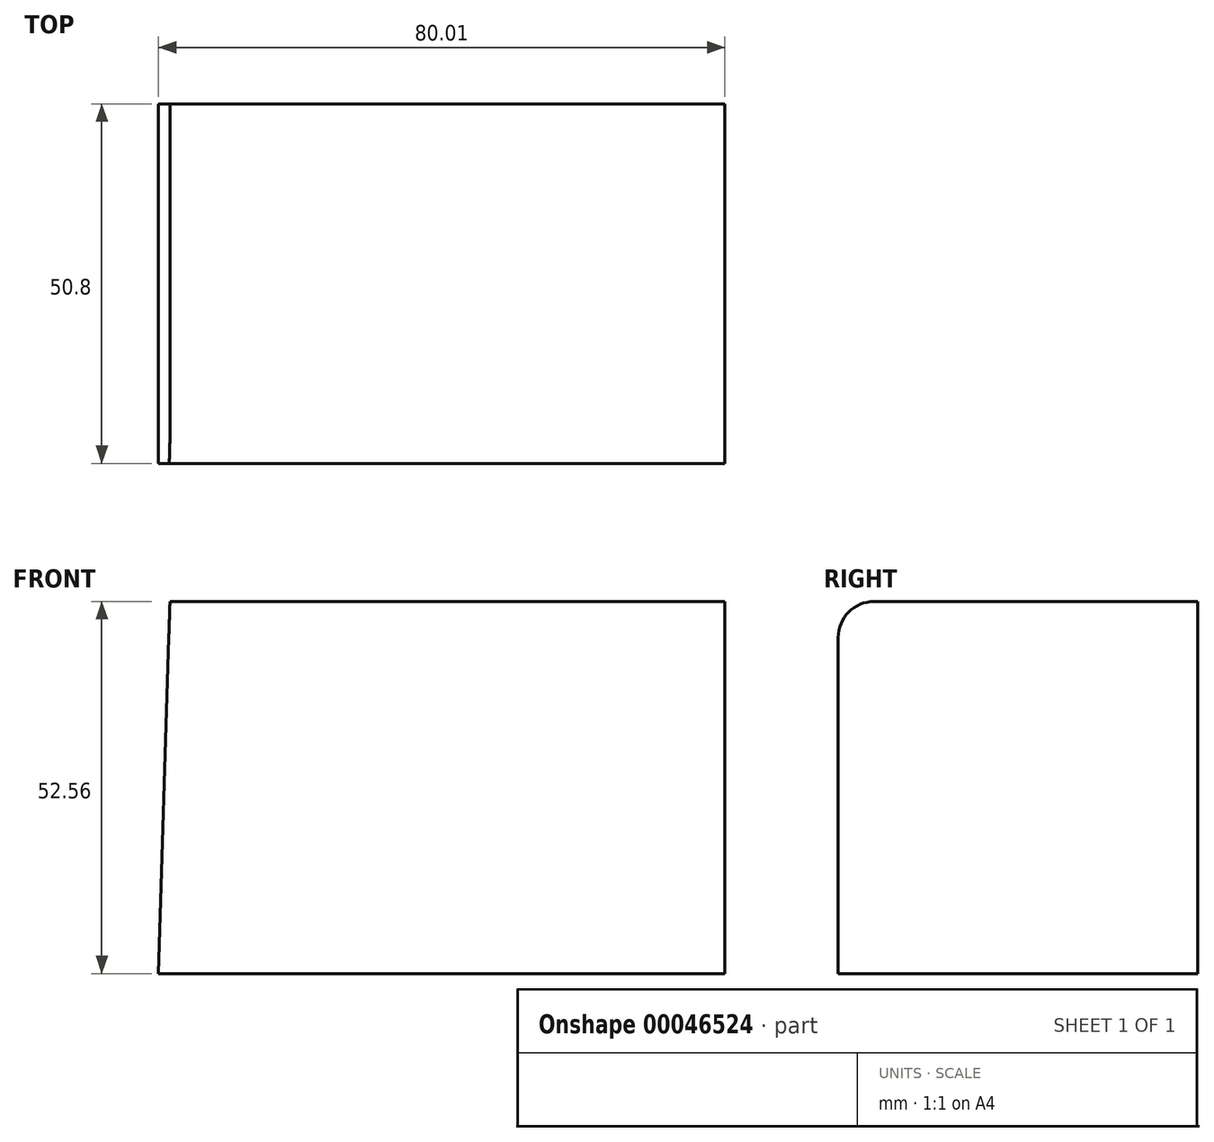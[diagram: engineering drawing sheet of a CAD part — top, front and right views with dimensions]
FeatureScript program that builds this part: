
annotation { "Feature Type Name" : "Feature", "Feature Type Description" : "" }
export const myFeature = defineFeature(function(context is Context, id is Id, definition is map)
    precondition{}
    {
        {
            var Q0;
            Q0=qCreatedBy(makeId("Front.planeOp"),FACE);
            var sketch = newSketch(context, id + "F0", { "sketchPlane" : qUnion([Q0])});
            skLineSegment(sketch, "E0", {"start": v(-41.16, 30.4) * mm, "end": v(38.85, 30.4) * mm});
            skLineSegment(sketch, "E1", {"start": v(38.85, 30.4) * mm, "end": v(38.85, 82.96) * mm});
            skLineSegment(sketch, "E2", {"start": v(38.85, 82.96) * mm, "end": v(-39.54, 82.96) * mm});
            skLineSegment(sketch, "E3", {"start": v(-39.54, 82.96) * mm, "end": v(-41.16, 30.4) * mm});
            skSolve(sketch);
        }
        {
            var Q0;
            Q0 = qSketchRegion(id + "F0", true);
            extrude(context, id + "F1", {"entities" : qUnion([Q0]), "depth" : 50.8 * mm});
        }
        {
            var Q0;
            Q0=makeQuery(id+"F1.opExtrude","CAP_EDGE",EDGE,{"disambiguationData":[OSD([sQuery(id+"F0.wireOp",EDGE,"E2")])],"isStart":false});
            fillet(context, id + "F2", {"entities" : qUnion([Q0]), "radius" : 5.08 * mm, "tangentPropagation" : true, "allowEdgeOverflow" : false});
        }
    });
